# Revit family: 6273_Klemmset G1 (metallisch dichtend)
name_source: partatom
category: Rohrformteile
units: mm (PartAtom-declared; Revit-internal decimal feet)

## family parameters
Arbeitsebenenbasiert = Nein
Beim Laden mit Abzugskörper schneiden = Nein
Bemaßung runder Anschluss = Durchmesser verwenden
Gemeinsam genutzt = Nein
Immer vertikal = Ja
OmniClass-Nummer = 23.65.55.14
OmniClass-Titel = Valves for Liquid Services
Teiletyp = Verbindung

## types (1)
- G1 x 22mm
    Anwendungsgebiet = Der Klemmring stellt eine absolut sichere Verbindung zwischen dem Ventilgehäuse und dem Rohr dar.
Diese Verbindung eignet sich besonders für Kupferrohre und dünnwandige Stahlrohre und kann bei Bedarf jederzeit gelöst werden.
Eine einwandfreie Dichtheit auf Dauer ist dann gegeben, wenn die Montage gemäß der Verarbeitungsanleitung durchgeführt wurde.


Nach Anzug der Klemmschraube verkeilt sich der Klemmring zwischen Rohrwand und Innenkonus von Gehäuse und Klemmschraube.
Dabei wird das Rohr in seiner Lage durch Kraftschluss fixiert und gegen Axialverschiebung gesichert.
Die dabei entstehende Pressung sorgt für sichere Dichtheit.
Die innen im Klemmring befindlichen Rillen stellen eine Labyrinthdichtung dar und helfen Unebenheiten des Rohres zu überbrücken.

Die Klemmverschraubung kann mehrmals gelöst werden und stellt eine einfache und sichere Verbindung dar.
Für die Güte der Verbindung ist es wichtig, dass das Rohr gegen den Anschlag im Innenkonus stößt, also ausreichend tief eingeschoben ist.

Die asymetrischen Klemmringe (6274, 6284, 6294) mit integrierten Reduzierhüllen ermöglichen den Rohranschluss von Rohren mit Durchmesser 8 - 16mm an einen Ventilkörper.
Diese Ausführung stellt ein Optimum an Kombinationsmöglichkeiten sicher.
    Ausführung = 6273 G1 - 22mm:
Klemmring mit aufgezogenem O- Ring, metallisch dichtend zum Rohr, Klemmringmutter G1 vernickelt, inkl. Stützhülse;
Einsetzbar für Weichtstahl- und Kupferrohre.
Nicht geeignet für verchromte Metallrohre oder Edelstahlrohre
.
    Hersteller = HERZ Armaturen Ges.m.b.H.
    KH00 = 1 mm  [stored 0.00328084 ft]
    KH01 = 0.9 mm  [stored 0.00295276 ft]
    KL00 = 18.1 mm  [stored 0.0593832 ft]
    KL01 = 5 mm  [stored 0.0164042 ft]
    KL02 = 6.6 mm  [stored 0.0216535 ft]
    KL03 = 12.9 mm  [stored 0.0423228 ft]
    KL04 = 14.7 mm  [stored 0.0482283 ft]
    Klemmring = CW602N
    MD01 = 19 mm  [stored 0.062336 ft]
    MD02 = 15 mm  [stored 0.0492126 ft]
    MD03 = 11.1 mm  [stored 0.0364173 ft]
    MD04 = 9.53 mm
    ML00 = 20 mm  [stored 0.0656168 ft]
    ML01 = 15 mm  [stored 0.0492126 ft]
    Max. Betriebsdruck = gemäß EN 1254-2: 1988, Tabelle 5
    Max. Betriebstemperatur = 110 °C
    Medium = Heizungswasser nach ÖNORM H5195 oder VDI- Richtlinie 2035.
Die Verwendung von Ethylen- oder Propyleneglykol in einem Mischungsverhältnis 25- 50% ist zulässig.
    Mutter = CW602N, G1 ISO 228-1
    Nennweite_Kupfer = 22 mm  [stored 0.0721785 ft]
    Nennweite_Stahl = 25 mm  [stored 0.082021 ft]
    S01 = 5 mm  [stored 0.0164042 ft]
    S02 = 5 mm  [stored 0.0164042 ft]
    SCRNCODE = 07;01;02
    SCRNSEQ = AWI;AWI_TYP="1001";2
    URL = www.herz-armaturen.at
    Vorgabe-Ansicht = 0 mm  [stored 0 ft]
    W01 = 30.00°
    W02 = 45.00°

note: [stored X ft] marks values corroborated as IEEE doubles in the binary element streams (Revit-internal decimal feet)
